# Revit family: DONA LED 18W RGB_LKB0918RGB.25
name_source: partatom
category: Luminarias
units: mm (PartAtom-declared; Revit-internal decimal feet)

## family parameters
Compartido = No
Corte con vacíos al cargar = No
Cota de conector redondo = Diámetro de uso
Origen de luz = Sí
Punto de cálculo de habitación = No
Se basa en plano de trabajo = Sí
Siempre vertical = No
Tipo de pieza = Normal

## types (2) — shared parameters
Cambio de temperatura de color de luz atenuada = <Ninguno>
Carga aparente = 0 VA
Fabricante = BRILLANT
Filtro de color = 16777215
Ángulo de inclinación = 60.00°
zero-valued in all types: Elevación por defecto

## per-type parameters (varying)
| type | Archivo de red fotométrica | Comentarios de vataje | Descripción | Lámpara | Modelo | Watt per fixture |
| SUB_LKB0918RGB.25 | LKB0918RGB.IES | 24V | LUMINARIA SUB ACUATICA TIPO PUNTUAL PARA EMPOTRAR EN PISO 180MM DE DIAMETRO POR 120MM DE ALTO CONSIDERANDO EL HOUSING, EN FORMA DE DONA, IDEAL PARA FUENTES O CHORROS DE AGUA, ACABADO EN ACERO INOXIDABLE, CUERPO MOLDEADO EN CROMO, SELLO DE SILICON, VIDRIO TEMPLADO DE 8MM, 9 LED TIPO OSRAM CON UN CONSUMO TOTAL DE 25.2W, 580 LUMENES, IP 68, IK 08, SUMERGIBLE MAXIMO 2M, CABLE H07RN DE 3M, APERTURA DE 25 GRADOS, ALIMENTADA A 24V. REQUIERE ACCESORIOS. | RGB | LKB0918RGB.25 | 25.2 |
| SUB_LKPB0158CW | generic | 24 | LUMINARIA SUB ACUATICA TIPO PUNTUAL, ACABADO EN ACERO INOXIDABLE, CUPERO MOLDEADO EN CROMO, SELLO DE SILICON, VIDRIO TEMPLADO DE 7MM, 1 LED TIPO OSRAM CON UN CONSUMO TOTAL DE 3W, 174 LUMENES CON  UNA TEMPERATURA EN BLANCO FRIO 6000K, IP 68, IK 06, SUMERGIBLE MAXIMO 2M, CABLE H07RN DE 3M, ALIMENTADA A 24V. REQUIERE ACCESORIOS. | Osram | LKPB0158CW | 3 |

## geometry (parser evidence)
native form markers: Blend x2
no freeform markers — native parametric forms only
